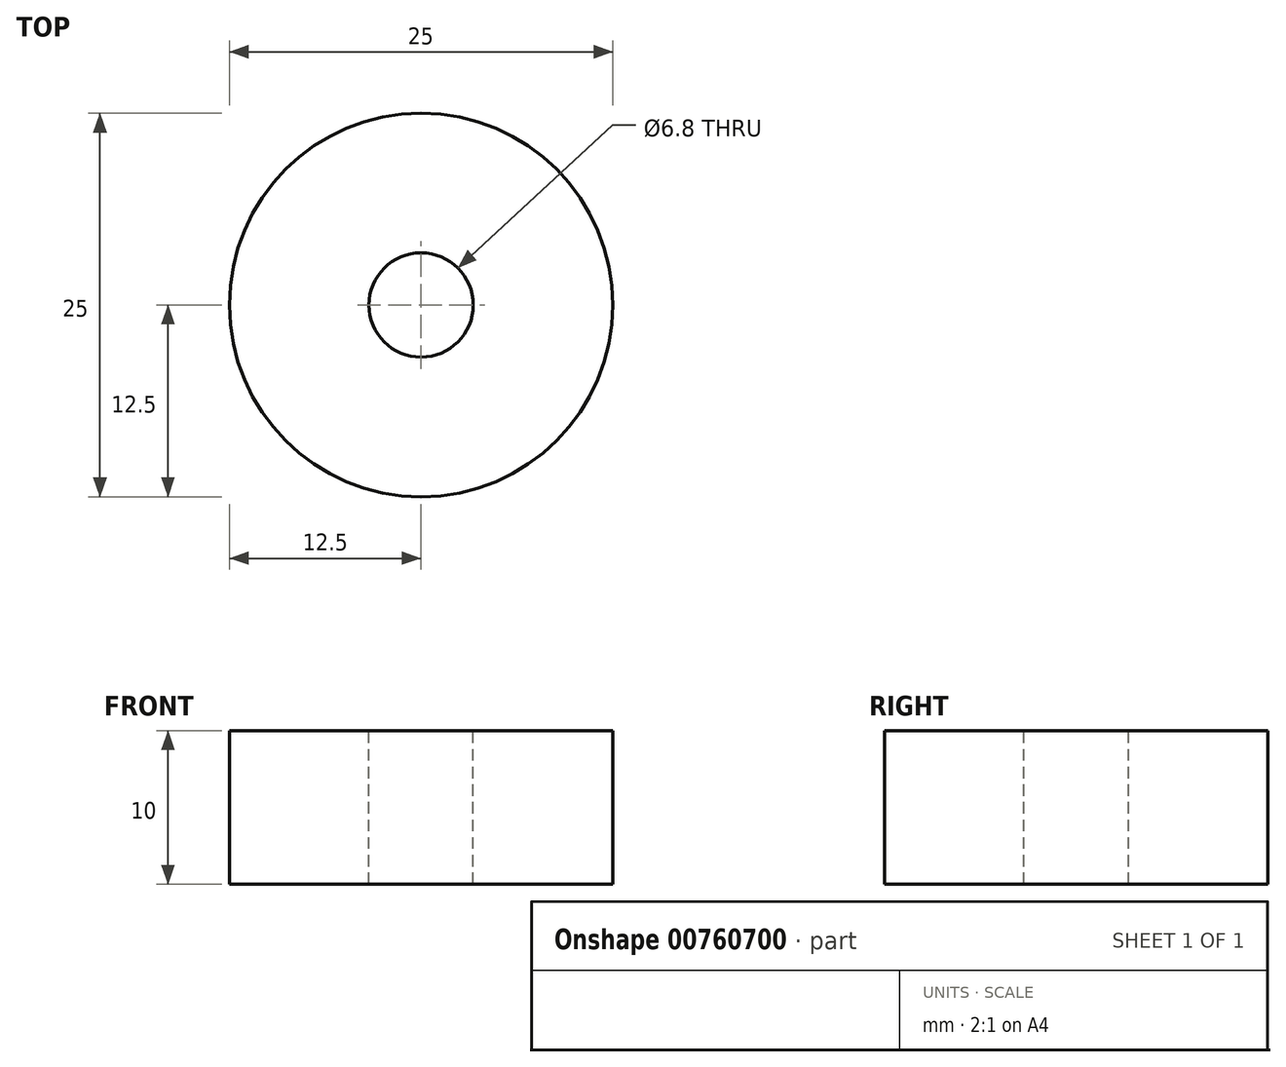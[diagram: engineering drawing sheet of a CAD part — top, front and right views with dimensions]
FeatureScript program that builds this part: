
annotation { "Feature Type Name" : "Feature", "Feature Type Description" : "" }
export const myFeature = defineFeature(function(context is Context, id is Id, definition is map)
    precondition{}
    {
        {
            var Q0;
            Q0=qCreatedBy(makeId("Top.planeOp"),FACE);
            var sketch = newSketch(context, id + "F0", { "sketchPlane" : qUnion([Q0])});
            skCircle(sketch, "E0", {"center": v(0, 0) * mm, "radius": 12.5 * mm});
            skSolve(sketch);
        }
        {
            var Q0;
            Q0=makeQuery(id+"F0.imprint","IMPRINT",FACE,{"disambiguationData":[TD([[makeQuery(id+"F0.imprint","IMPRINT",EDGE,{"derivedFrom":sQuery(id+"F0.wireOp",EDGE,"E0")}),1.0]])]});
            var Q1;
            Q1=sQuery(id+"F0.wireOp",EDGE,"E0");
            extrude(context, id + "F1", {"entities" : qUnion([Q0]), "surfaceEntities" : qUnion([Q1]), "depth" : 10 * mm, "offsetDistance" : 25 * mm});
        }
        {
            var Q0;
            Q0=makeQuery(id+"F1.opExtrude","CAP_FACE",FACE,{"disambiguationData":[OSD([sQuery(id+"F0.wireOp",EDGE,"E0")])],"isStart":false});
            var sketch = newSketch(context, id + "F2", { "sketchPlane" : qUnion([Q0])});
            skCircle(sketch, "E1", {"center": v(0, 0) * mm, "radius": 3.4 * mm});
            skSolve(sketch);
        }
        {
            var Q0;
            Q0=makeQuery(id+"F2.imprint","IMPRINT",FACE,{"disambiguationData":[TD([[makeQuery(id+"F2.imprint","IMPRINT",EDGE,{"derivedFrom":sQuery(id+"F2.wireOp",EDGE,"E1")}),1.0]])]});
            extrude(context, id + "F3", {"entities" : qUnion([Q0]), "operationType" : NewBodyOperationType.REMOVE, "endBound" : BoundingType.THROUGH_ALL, "oppositeDirection" : true, "depth" : 25 * mm, "offsetDistance" : 25 * mm});
        }
    });
